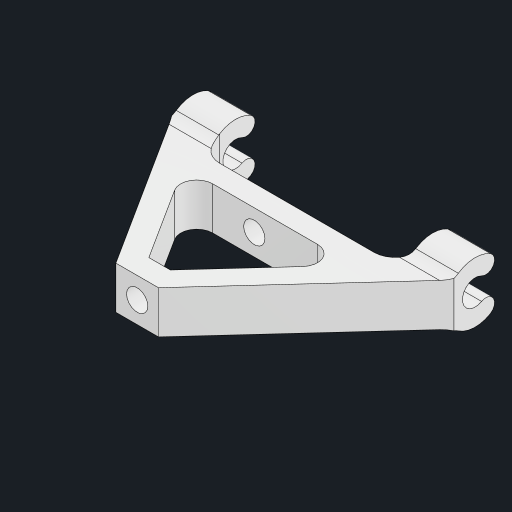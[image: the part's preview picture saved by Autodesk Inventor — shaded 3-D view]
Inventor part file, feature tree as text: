
AUTODESK INVENTOR PART (.ipt)
format: ipt  version: 2023 (Build 270158000, 158)  size: 207,360 bytes
history: native  units: mm
features: sketch x4, extrude x4, fillet x2, other x1, hole x1, mirror x1
ambient origin geometry x8: Origin, YZ Plane, XZ Plane, XY Plane, X Axis, Y Axis, Z Axis, Center Point
bodies: Body1 (feature_tree)
feature tree (13):
  other  "ソリッド1"
  sketch  "スケッチ1"
  extrude  "押し出し1"  Depth=4.0mm
  hole  "穴1"  [1 undecoded]
  sketch  "スケッチ4"
  extrude  "押し出し3"  Depth=16.5mm
  extrude  "押し出し4"  Depth=4.0mm TaperAngle=0.0deg
  mirror  "ミラー1"
  extrude  "押し出し5"  Depth=3.5mm
  fillet  "フィレット4"  Radius=2.4mm
  fillet  "フィレット5"  [1 undecoded]
  sketch  "スケッチ3"
  sketch  "スケッチ5"
note: 2 required parameter values undecoded (feature->parameter linkage not recoverable at this tier; creation-order binding heuristic only, values carry confidence <= 0.55)
